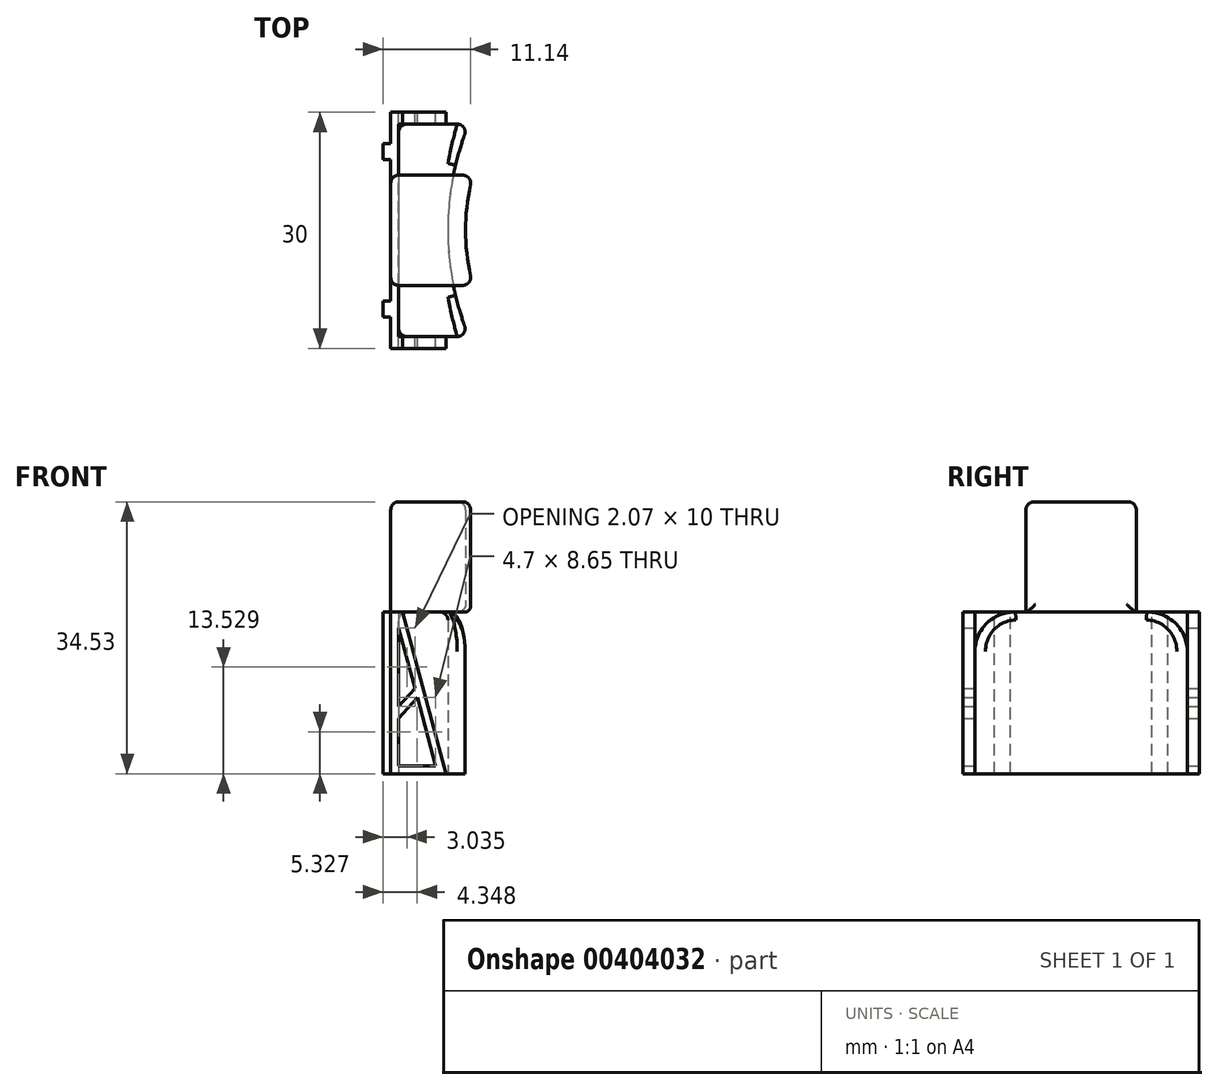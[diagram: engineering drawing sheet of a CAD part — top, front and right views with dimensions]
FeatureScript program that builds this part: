
annotation { "Feature Type Name" : "Feature", "Feature Type Description" : "" }
export const myFeature = defineFeature(function(context is Context, id is Id, definition is map)
    precondition{}
    {
        {
            var Q0;
            Q0=qCreatedBy(makeId("Front.planeOp"),FACE);
            var sketch = newSketch(context, id + "F0", { "sketchPlane" : qUnion([Q0])});
            skLineSegment(sketch, "E0", {"start": v(0, 0) * mm, "end": v(0, 20.53) * mm});
            skLineSegment(sketch, "E1", {"start": v(0, 20.53) * mm, "end": v(1.5, 20.53) * mm});
            skLineSegment(sketch, "E2", {"start": v(1.5, 20.53) * mm, "end": v(7, 0) * mm});
            skLineSegment(sketch, "E3", {"start": v(7, 0) * mm, "end": v(0, 0) * mm});
            skSolve(sketch);
        }
        {
            var Q0;
            Q0 = qSketchRegion(id + "F0", true);
            extrude(context, id + "F1", {"entities" : qUnion([Q0]), "endBound" : BoundingType.SYMMETRIC, "depth" : 30 * mm});
        }
        {
            var Q0;
            Q0=qCreatedBy(makeId("Top.planeOp"),FACE);
            var sketch = newSketch(context, id + "F2", { "sketchPlane" : qUnion([Q0])});
            skLineSegment(sketch, "E4.bottom", {"start": v(1, 13.5) * mm, "end": v(8, 13.5) * mm});
            skLineSegment(sketch, "E4.top", {"start": v(1, -13.5) * mm, "end": v(8, -13.5) * mm});
            skLineSegment(sketch, "E4.left", {"start": v(1, 13.5) * mm, "end": v(1, -13.5) * mm});
            skLineSegment(sketch, "E4.right", {"start": v(8, 13.5) * mm, "end": v(8, -13.5) * mm});
            skSolve(sketch);
        }
        {
            var Q0;
            Q0 = qSketchRegion(id + "F2", true);
            extrude(context, id + "F3", {"entities" : qUnion([Q0]), "depth" : 25 * mm});
        }
        {
            var Q0;
            Q0=qCreatedBy(makeId("Front.planeOp"),FACE);
            var sketch = newSketch(context, id + "F4", { "sketchPlane" : qUnion([Q0])});
            skLineSegment(sketch, "E5", {"start": v(1, 18.53) * mm, "end": v(1, 8.53) * mm});
            skLineSegment(sketch, "E6", {"start": v(1, 8.53) * mm, "end": v(3.07, 10.8) * mm});
            skLineSegment(sketch, "E7", {"start": v(3.07, 10.8) * mm, "end": v(1, 18.53) * mm});
            skSolve(sketch);
        }
        {
            var Q0;
            Q0=qCreatedBy(makeId("Front.planeOp"),FACE);
            var sketch = newSketch(context, id + "F5", { "sketchPlane" : qUnion([Q0])});
            skLineSegment(sketch, "E8", {"start": v(1, 7.04) * mm, "end": v(1, 1) * mm});
            skLineSegment(sketch, "E9", {"start": v(1, 1) * mm, "end": v(5.7, 1) * mm});
            skLineSegment(sketch, "E10", {"start": v(5.7, 1) * mm, "end": v(3.38, 9.65) * mm});
            skLineSegment(sketch, "E11", {"start": v(3.38, 9.65) * mm, "end": v(1, 7.04) * mm});
            skSolve(sketch);
        }
        {
            var Q0;
            Q0 = qSketchRegion(id + "F4", true);
            var Q1;
            Q1 = qSketchRegion(id + "F5", true);
            extrude(context, id + "F6", {"entities" : qUnion([Q0, Q1]), "endBound" : BoundingType.SYMMETRIC, "depth" : 40 * mm});
        }
        {
            var Q0;
            Q0=makeQuery(id+"F6.opExtrude","SWEPT_BODY",BODY,{"disambiguationData":[OSD([sQuery(id+"F5.wireOp",EDGE,"E8"),sQuery(id+"F5.wireOp",EDGE,"E9"),sQuery(id+"F5.wireOp",EDGE,"E10"),sQuery(id+"F5.wireOp",EDGE,"E11")])]});
            var Q1;
            Q1=makeQuery(id+"F6.opExtrude","SWEPT_BODY",BODY,{"disambiguationData":[OSD([sQuery(id+"F4.wireOp",EDGE,"E5"),sQuery(id+"F4.wireOp",EDGE,"E6"),sQuery(id+"F4.wireOp",EDGE,"E7")])]});
            var Q2;
            Q2=makeQuery(id+"F3.opExtrude","SWEPT_BODY",BODY,{"disambiguationData":[OSD([sQuery(id+"F2.wireOp",EDGE,"E4.bottom"),sQuery(id+"F2.wireOp",EDGE,"E4.top"),sQuery(id+"F2.wireOp",EDGE,"E4.left"),sQuery(id+"F2.wireOp",EDGE,"E4.right")])]});
            var Q3;
            Q3=makeQuery(id+"F1.opExtrude","SWEPT_BODY",BODY,{"disambiguationData":[OSD([sQuery(id+"F0.wireOp",EDGE,"E0"),sQuery(id+"F0.wireOp",EDGE,"E1"),sQuery(id+"F0.wireOp",EDGE,"E2"),sQuery(id+"F0.wireOp",EDGE,"E3")])]});
            booleanBodies(context, id + "F7", {"operationType" : BooleanOperationType.SUBTRACTION, "tools" : qUnion([Q0, Q1, Q2]), "targets" : qUnion([Q3])});
        }
        {
            var Q0;
            Q0=makeQuery(id+"F1.opExtrude","SWEPT_FACE",FACE,{"disambiguationData":[OSD([sQuery(id+"F0.wireOp",EDGE,"E1")])]});
            var sketch = newSketch(context, id + "F8", { "sketchPlane" : qUnion([Q0])});
            skLineSegment(sketch, "E12.bottom", {"start": v(0, -9) * mm, "end": v(-1, -9) * mm});
            skLineSegment(sketch, "E12.top", {"start": v(0, -11) * mm, "end": v(-1, -11) * mm});
            skLineSegment(sketch, "E12.left", {"start": v(0, -9) * mm, "end": v(0, -11) * mm});
            skLineSegment(sketch, "E12.right", {"start": v(-1, -9) * mm, "end": v(-1, -11) * mm});
            skPoint(sketch, "E13.oppositeSnap0", {"position": v(-1, -10) * mm});
            skLineSegment(sketch, "E13.bottom", {"start": v(0, 11) * mm, "end": v(-1, 11) * mm});
            skLineSegment(sketch, "E13.top", {"start": v(0, 9) * mm, "end": v(-1, 9) * mm});
            skLineSegment(sketch, "E13.left", {"start": v(0, 11) * mm, "end": v(0, 9) * mm});
            skLineSegment(sketch, "E13.right", {"start": v(-1, 11) * mm, "end": v(-1, 9) * mm});
            skSolve(sketch);
        }
        {
            var Q0;
            Q0 = qSketchRegion(id + "F8", true);
            var Q1;
            Q1=makeQuery(id+"F1.opExtrude","SWEPT_FACE",FACE,{"disambiguationData":[OSD([sQuery(id+"F0.wireOp",EDGE,"E3")])]});
            extrude(context, id + "F9", {"entities" : qUnion([Q0]), "operationType" : NewBodyOperationType.ADD, "endBound" : BoundingType.UP_TO_SURFACE, "oppositeDirection" : true, "endBoundEntityFace" : qUnion([Q1]), "depth" : 20 * mm});
        }
        {
            var Q0;
            Q0=qCreatedBy(makeId("Top.planeOp"),FACE);
            var sketch = newSketch(context, id + "F10", { "sketchPlane" : qUnion([Q0])});
            skLineSegment(sketch, "E14.bottom", {"start": v(1, 13.5) * mm, "end": v(10, 13.5) * mm});
            skLineSegment(sketch, "E14.top", {"start": v(1, -13.5) * mm, "end": v(10, -13.5) * mm});
            skLineSegment(sketch, "E14.left", {"start": v(1, 13.5) * mm, "end": v(1, -13.5) * mm});
            skLineSegment(sketch, "E14.right", {"start": v(10, 13.5) * mm, "end": v(10, -13.5) * mm});
            skSolve(sketch);
        }
        {
            var Q0;
            Q0 = qSketchRegion(id + "F10", true);
            var Q1;
            Q1=makeQuery(id+"F9.boolean.opBoolean","MERGE",FACE,{"derivedFrom":[makeQuery(id+"F1.opExtrude","SWEPT_FACE",FACE,{"disambiguationData":[OSD([sQuery(id+"F0.wireOp",EDGE,"E1")])]}),makeQuery(id+"F9.opExtrude","CAP_FACE",FACE,{"disambiguationData":[OSD([sQuery(id+"F8.wireOp",EDGE,"E12.bottom"),sQuery(id+"F8.wireOp",EDGE,"E12.top"),sQuery(id+"F8.wireOp",EDGE,"E12.left"),sQuery(id+"F8.wireOp",EDGE,"E12.right")])],"isStart":true}),makeQuery(id+"F9.opExtrude","CAP_FACE",FACE,{"disambiguationData":[OSD([sQuery(id+"F8.wireOp",EDGE,"E13.bottom"),sQuery(id+"F8.wireOp",EDGE,"E13.top"),sQuery(id+"F8.wireOp",EDGE,"E13.left"),sQuery(id+"F8.wireOp",EDGE,"E13.right")])],"isStart":true})]});
            extrude(context, id + "F11", {"entities" : qUnion([Q0]), "endBound" : BoundingType.UP_TO_SURFACE, "endBoundEntityFace" : qUnion([Q1]), "depth" : 25 * mm});
        }
        {
            var Q0;
            Q0=qCreatedBy(makeId("Top.planeOp"),FACE);
            var sketch = newSketch(context, id + "F12", { "sketchPlane" : qUnion([Q0])});
            skCircle(sketch, "E15", {"center": v(43, 0) * mm, "radius": 35.75 * mm});
            skSolve(sketch);
        }
        {
            var Q0;
            Q0 = qSketchRegion(id + "F12", true);
            extrude(context, id + "F13", {"entities" : qUnion([Q0]), "depth" : 30 * mm});
        }
        {
            var Q0;
            Q0=makeQuery(id+"F13.opExtrude","SWEPT_BODY",BODY,{"disambiguationData":[OSD([sQuery(id+"F12.wireOp",EDGE,"E15")])]});
            var Q1;
            Q1=makeQuery(id+"F11.opExtrude","SWEPT_BODY",BODY,{"disambiguationData":[OSD([sQuery(id+"F10.wireOp",EDGE,"E14.bottom"),sQuery(id+"F10.wireOp",EDGE,"E14.top"),sQuery(id+"F10.wireOp",EDGE,"E14.left"),sQuery(id+"F10.wireOp",EDGE,"E14.right")])]});
            booleanBodies(context, id + "F14", {"operationType" : BooleanOperationType.SUBTRACTION, "tools" : qUnion([Q0]), "targets" : qUnion([Q1])});
        }
        {
            var Q0;
            Q0=makeQuery(id+"F11.opExtrude","CAP_EDGE",EDGE,{"disambiguationData":[OSD([sQuery(id+"F10.wireOp",EDGE,"E14.top")])],"isStart":false});
            var Q1;
            Q1=makeQuery(id+"F11.opExtrude","CAP_EDGE",EDGE,{"disambiguationData":[OSD([sQuery(id+"F10.wireOp",EDGE,"E14.bottom")])],"isStart":false});
            fillet(context, id + "F15", {"entities" : qUnion([Q0, Q1]), "radius" : 5 * mm, "tangentPropagation" : true, "allowEdgeOverflow" : false});
        }
        {
            var Q0;
            Q0=makeQuery(id+"F14.opBoolean","INTERSECT",EDGE,{"derivedFrom":[makeQuery(id+"F11.opExtrude","SWEPT_FACE",FACE,{"disambiguationData":[OSD([sQuery(id+"F10.wireOp",EDGE,"E14.top")])]}),makeQuery(id+"F13.opExtrude","SWEPT_FACE",FACE,{"disambiguationData":[OSD([sQuery(id+"F12.wireOp",EDGE,"E15")])]})]});
            var Q1;
            Q1=makeQuery(id+"F11.opExtrude","SWEPT_EDGE",EDGE,{"disambiguationData":[OSD([sQuery(id+"F10.wireOp",EDGE,"E14.top"),sQuery(id+"F10.wireOp",EDGE,"E14.left")])]});
            fillet(context, id + "F16", {"entities" : qUnion([Q0, Q1]), "radius" : 1 * mm, "tangentPropagation" : true, "allowEdgeOverflow" : false});
        }
        {
            var Q0;
            Q0=makeQuery(id+"F11.opExtrude","CAP_FACE",FACE,{"disambiguationData":[OSD([sQuery(id+"F10.wireOp",EDGE,"E14.bottom"),sQuery(id+"F10.wireOp",EDGE,"E14.top"),sQuery(id+"F10.wireOp",EDGE,"E14.left"),sQuery(id+"F10.wireOp",EDGE,"E14.right")])],"isStart":false});
            var sketch = newSketch(context, id + "F17", { "sketchPlane" : qUnion([Q0])});
            skLineSegment(sketch, "E16.bottom", {"start": v(0, 7) * mm, "end": v(11, 7) * mm});
            skLineSegment(sketch, "E16.top", {"start": v(0, -7) * mm, "end": v(11, -7) * mm});
            skLineSegment(sketch, "E16.left", {"start": v(0, 7) * mm, "end": v(0, -7) * mm});
            skLineSegment(sketch, "E16.right", {"start": v(11, 7) * mm, "end": v(11, -7) * mm});
            skSolve(sketch);
        }
        {
            var Q0;
            Q0 = qSketchRegion(id + "F17", true);
            extrude(context, id + "F18", {"entities" : qUnion([Q0]), "depth" : 14 * mm});
        }
        {
            var Q0;
            Q0=qCreatedBy(makeId("Top.planeOp"),FACE);
            var sketch = newSketch(context, id + "F19", { "sketchPlane" : qUnion([Q0])});
            skCircle(sketch, "E17", {"center": v(37, 0) * mm, "radius": 27.5 * mm});
            skSolve(sketch);
        }
        {
            var Q0;
            Q0 = qSketchRegion(id + "F19", true);
            extrude(context, id + "F20", {"entities" : qUnion([Q0]), "depth" : 60 * mm});
        }
        {
            var Q0;
            Q0=makeQuery(id+"F20.opExtrude","SWEPT_BODY",BODY,{"disambiguationData":[OSD([sQuery(id+"F19.wireOp",EDGE,"E17")])]});
            var Q1;
            Q1=makeQuery(id+"F18.opExtrude","SWEPT_BODY",BODY,{"disambiguationData":[OSD([sQuery(id+"F17.wireOp",EDGE,"E16.bottom"),sQuery(id+"F17.wireOp",EDGE,"E16.top"),sQuery(id+"F17.wireOp",EDGE,"E16.left"),sQuery(id+"F17.wireOp",EDGE,"E16.right")])]});
            booleanBodies(context, id + "F21", {"operationType" : BooleanOperationType.SUBTRACTION, "tools" : qUnion([Q0]), "targets" : qUnion([Q1])});
        }
        {
            var Q0;
            Q0=makeQuery(id+"F21.opBoolean","COPY",FACE,{"derivedFrom":makeQuery(id+"F20.opExtrude","SWEPT_FACE",FACE,{"disambiguationData":[OSD([sQuery(id+"F19.wireOp",EDGE,"E17")])]})});
            var Q1;
            Q1=makeQuery(id+"F18.opExtrude","CAP_EDGE",EDGE,{"disambiguationData":[OSD([sQuery(id+"F17.wireOp",EDGE,"E16.bottom")])],"isStart":false});
            var Q2;
            Q2=makeQuery(id+"F18.opExtrude","CAP_EDGE",EDGE,{"disambiguationData":[OSD([sQuery(id+"F17.wireOp",EDGE,"E16.top")])],"isStart":false});
            var Q3;
            Q3=makeQuery(id+"F18.opExtrude","CAP_EDGE",EDGE,{"disambiguationData":[OSD([sQuery(id+"F17.wireOp",EDGE,"E16.left")])],"isStart":false});
            var Q4;
            Q4=makeQuery(id+"F18.opExtrude","SWEPT_EDGE",EDGE,{"disambiguationData":[OSD([sQuery(id+"F17.wireOp",EDGE,"E16.bottom"),sQuery(id+"F17.wireOp",EDGE,"E16.left")])]});
            var Q5;
            Q5=makeQuery(id+"F18.opExtrude","SWEPT_EDGE",EDGE,{"disambiguationData":[OSD([sQuery(id+"F17.wireOp",EDGE,"E16.top"),sQuery(id+"F17.wireOp",EDGE,"E16.left")])]});
            fillet(context, id + "F22", {"entities" : qUnion([Q0, Q1, Q2, Q3, Q4, Q5]), "radius" : 1 * mm, "tangentPropagation" : true, "allowEdgeOverflow" : false});
        }
    });
